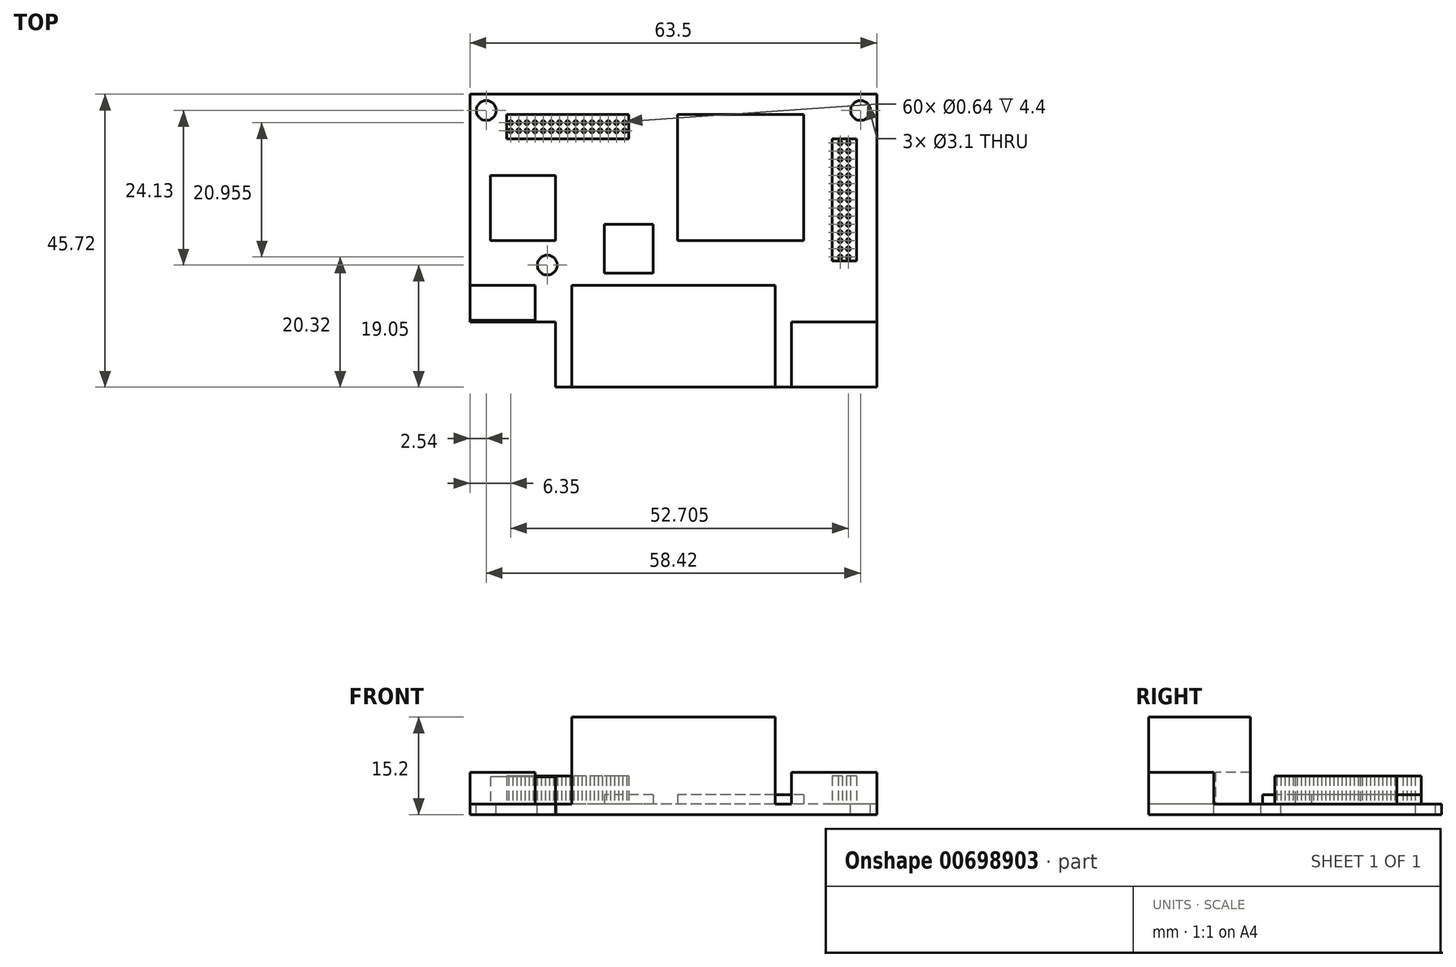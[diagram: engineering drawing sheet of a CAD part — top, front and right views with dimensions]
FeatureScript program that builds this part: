
annotation { "Feature Type Name" : "Feature", "Feature Type Description" : "" }
export const myFeature = defineFeature(function(context is Context, id is Id, definition is map)
    precondition{}
    {
        {
            var Q0;
            Q0=qCreatedBy(makeId("Top.planeOp"),FACE);
            var sketch = newSketch(context, id + "F0", { "sketchPlane" : qUnion([Q0])});
            skLineSegment(sketch, "E0.bottom", {"start": v(31.75, 22.86) * mm, "end": v(-31.75, 22.86) * mm});
            skLineSegment(sketch, "E0.top", {"start": v(31.75, -22.86) * mm, "end": v(-31.75, -22.86) * mm});
            skLineSegment(sketch, "E0.left", {"start": v(31.75, 22.86) * mm, "end": v(31.75, -22.86) * mm});
            skLineSegment(sketch, "E0.right", {"start": v(-31.75, 22.86) * mm, "end": v(-31.75, -22.86) * mm});
            skPoint(sketch, "E0.middle", {"position": v(0, 0) * mm});
            skCircle(sketch, "E1", {"center": v(-29.21, 20.32) * mm, "radius": 1.55 * mm});
            skCircle(sketch, "E2", {"center": v(29.21, 20.32) * mm, "radius": 1.55 * mm});
            skCircle(sketch, "E3", {"center": v(-19.69, -3.81) * mm, "radius": 1.55 * mm});
            skLineSegment(sketch, "E4.bottom", {"start": v(-18.41, 10.16) * mm, "end": v(-28.57, 10.16) * mm});
            skLineSegment(sketch, "E4.top", {"start": v(-18.41, 0) * mm, "end": v(-28.57, 0) * mm});
            skLineSegment(sketch, "E4.left", {"start": v(-18.41, 10.16) * mm, "end": v(-18.41, 0) * mm});
            skLineSegment(sketch, "E4.right", {"start": v(-28.57, 10.16) * mm, "end": v(-28.57, 0) * mm});
            skPoint(sketch, "E4.middle", {"position": v(-23.5, 5.08) * mm});
            skLineSegment(sketch, "E5.bottom", {"start": v(20.32, 19.69) * mm, "end": v(0.63, 19.69) * mm});
            skLineSegment(sketch, "E5.top", {"start": v(20.32, 0) * mm, "end": v(0.63, 0) * mm});
            skLineSegment(sketch, "E5.left", {"start": v(20.32, 19.69) * mm, "end": v(20.32, 0) * mm});
            skLineSegment(sketch, "E5.right", {"start": v(0.64, 19.69) * mm, "end": v(0.64, 0) * mm});
            skPoint(sketch, "E5.middle", {"position": v(10.48, 9.84) * mm});
            skLineSegment(sketch, "E6.bottom", {"start": v(-3.17, 2.54) * mm, "end": v(-10.8, 2.54) * mm});
            skLineSegment(sketch, "E6.top", {"start": v(-3.17, -5.08) * mm, "end": v(-10.8, -5.08) * mm});
            skLineSegment(sketch, "E6.left", {"start": v(-3.17, 2.54) * mm, "end": v(-3.17, -5.08) * mm});
            skLineSegment(sketch, "E6.right", {"start": v(-10.8, 2.54) * mm, "end": v(-10.8, -5.08) * mm});
            skPoint(sketch, "E6.middle", {"position": v(-6.98, -1.27) * mm});
            skLineSegment(sketch, "E7.bottom", {"start": v(-31.75, -22.86) * mm, "end": v(-18.41, -22.86) * mm});
            skLineSegment(sketch, "E7.top", {"start": v(-31.75, -12.7) * mm, "end": v(-18.42, -12.7) * mm});
            skLineSegment(sketch, "E7.left", {"start": v(-31.75, -22.86) * mm, "end": v(-31.75, -12.7) * mm});
            skLineSegment(sketch, "E7.right", {"start": v(-18.41, -22.86) * mm, "end": v(-18.41, -12.7) * mm});
            skPoint(sketch, "E7.middle", {"position": v(-25.08, -17.78) * mm});
            skLineSegment(sketch, "E8.bottom", {"start": v(-21.6, -6.99) * mm, "end": v(-31.75, -6.99) * mm});
            skLineSegment(sketch, "E8.top", {"start": v(-21.59, -12.45) * mm, "end": v(-31.75, -12.45) * mm});
            skLineSegment(sketch, "E8.left", {"start": v(-21.59, -6.99) * mm, "end": v(-21.59, -12.45) * mm});
            skLineSegment(sketch, "E8.right", {"start": v(-31.75, -6.99) * mm, "end": v(-31.75, -12.45) * mm});
            skPoint(sketch, "E8.middle", {"position": v(-26.67, -9.72) * mm});
            skLineSegment(sketch, "E9.bottom", {"start": v(31.75, -12.7) * mm, "end": v(18.41, -12.7) * mm});
            skLineSegment(sketch, "E9.top", {"start": v(31.75, -22.86) * mm, "end": v(18.41, -22.86) * mm});
            skLineSegment(sketch, "E9.left", {"start": v(31.75, -12.7) * mm, "end": v(31.75, -22.86) * mm});
            skLineSegment(sketch, "E9.right", {"start": v(18.41, -12.7) * mm, "end": v(18.41, -22.86) * mm});
            skPoint(sketch, "E9.middle", {"position": v(25.08, -17.78) * mm});
            skLineSegment(sketch, "E10.bottom", {"start": v(15.88, -6.99) * mm, "end": v(-15.88, -6.99) * mm});
            skLineSegment(sketch, "E10.top", {"start": v(15.88, -22.86) * mm, "end": v(-15.88, -22.86) * mm});
            skLineSegment(sketch, "E10.left", {"start": v(15.88, -6.99) * mm, "end": v(15.88, -22.86) * mm});
            skLineSegment(sketch, "E10.right", {"start": v(-15.88, -6.99) * mm, "end": v(-15.88, -22.86) * mm});
            skPoint(sketch, "E10.middle", {"position": v(0, -14.92) * mm});
            skCircle(sketch, "E11", {"center": v(-25.4, 18.41) * mm, "radius": 0.32 * mm});
            skCircle(sketch, "E12.1.0.0", {"center": v(-24.13, 18.41) * mm, "radius": 0.32 * mm});
            skCircle(sketch, "E12.2.0.0", {"center": v(-22.86, 18.41) * mm, "radius": 0.32 * mm});
            skCircle(sketch, "E12.3.0.0", {"center": v(-21.59, 18.41) * mm, "radius": 0.32 * mm});
            skCircle(sketch, "E12.4.0.0", {"center": v(-20.32, 18.41) * mm, "radius": 0.32 * mm});
            skCircle(sketch, "E12.5.0.0", {"center": v(-19.05, 18.41) * mm, "radius": 0.32 * mm});
            skCircle(sketch, "E12.6.0.0", {"center": v(-17.78, 18.41) * mm, "radius": 0.32 * mm});
            skCircle(sketch, "E12.7.0.0", {"center": v(-16.51, 18.41) * mm, "radius": 0.32 * mm});
            skCircle(sketch, "E12.8.0.0", {"center": v(-15.24, 18.41) * mm, "radius": 0.32 * mm});
            skCircle(sketch, "E12.9.0.0", {"center": v(-13.97, 18.41) * mm, "radius": 0.32 * mm});
            skCircle(sketch, "E12.10.0.0", {"center": v(-12.7, 18.41) * mm, "radius": 0.32 * mm});
            skCircle(sketch, "E12.11.0.0", {"center": v(-11.43, 18.41) * mm, "radius": 0.32 * mm});
            skCircle(sketch, "E12.12.0.0", {"center": v(-10.16, 18.41) * mm, "radius": 0.32 * mm});
            skCircle(sketch, "E12.13.0.0", {"center": v(-8.89, 18.41) * mm, "radius": 0.32 * mm});
            skCircle(sketch, "E12.14.0.0", {"center": v(-7.62, 18.41) * mm, "radius": 0.32 * mm});
            skLineSegment(sketch, "E12.direction1", {"start": v(-25.4, 18.41) * mm, "end": v(-24.13, 18.41) * mm, "construction": true});
            skCircle(sketch, "E13.1.0.0", {"center": v(-19.05, 17.14) * mm, "radius": 0.32 * mm});
            skCircle(sketch, "E13.1.0.1", {"center": v(-17.78, 17.14) * mm, "radius": 0.32 * mm});
            skCircle(sketch, "E13.1.0.2", {"center": v(-16.51, 17.14) * mm, "radius": 0.32 * mm});
            skCircle(sketch, "E13.1.0.3", {"center": v(-13.97, 17.14) * mm, "radius": 0.32 * mm});
            skCircle(sketch, "E13.1.0.4", {"center": v(-11.43, 17.14) * mm, "radius": 0.32 * mm});
            skCircle(sketch, "E13.1.0.5", {"center": v(-8.89, 17.14) * mm, "radius": 0.32 * mm});
            skCircle(sketch, "E13.1.0.6", {"center": v(-25.4, 17.15) * mm, "radius": 0.32 * mm});
            skCircle(sketch, "E13.1.0.7", {"center": v(-24.13, 17.15) * mm, "radius": 0.32 * mm});
            skCircle(sketch, "E13.1.0.8", {"center": v(-22.86, 17.14) * mm, "radius": 0.32 * mm});
            skCircle(sketch, "E13.1.0.9", {"center": v(-21.59, 17.14) * mm, "radius": 0.32 * mm});
            skCircle(sketch, "E13.1.0.10", {"center": v(-20.32, 17.14) * mm, "radius": 0.32 * mm});
            skLineSegment(sketch, "E13.1.0.11", {"start": v(-25.4, 17.14) * mm, "end": v(-24.13, 17.14) * mm, "construction": true});
            skCircle(sketch, "E13.1.0.12", {"center": v(-7.62, 17.14) * mm, "radius": 0.32 * mm});
            skCircle(sketch, "E13.1.0.13", {"center": v(-10.16, 17.14) * mm, "radius": 0.32 * mm});
            skCircle(sketch, "E13.1.0.14", {"center": v(-12.7, 17.14) * mm, "radius": 0.32 * mm});
            skCircle(sketch, "E13.1.0.15", {"center": v(-15.24, 17.14) * mm, "radius": 0.32 * mm});
            skLineSegment(sketch, "E13.direction1", {"start": v(-25.4, 18.41) * mm, "end": v(-25.4, 17.15) * mm, "construction": true});
            skCircle(sketch, "E14", {"center": v(26.04, -2.54) * mm, "radius": 0.32 * mm});
            skCircle(sketch, "E15.1.0.0", {"center": v(26.03, -1.27) * mm, "radius": 0.32 * mm});
            skCircle(sketch, "E15.2.0.0", {"center": v(26.04, 0) * mm, "radius": 0.32 * mm});
            skCircle(sketch, "E15.3.0.0", {"center": v(26.04, 1.27) * mm, "radius": 0.32 * mm});
            skCircle(sketch, "E15.4.0.0", {"center": v(26.04, 2.54) * mm, "radius": 0.32 * mm});
            skCircle(sketch, "E15.5.0.0", {"center": v(26.04, 3.8) * mm, "radius": 0.32 * mm});
            skCircle(sketch, "E15.6.0.0", {"center": v(26.04, 5.08) * mm, "radius": 0.32 * mm});
            skCircle(sketch, "E15.7.0.0", {"center": v(26.04, 6.35) * mm, "radius": 0.32 * mm});
            skCircle(sketch, "E15.8.0.0", {"center": v(26.04, 7.62) * mm, "radius": 0.32 * mm});
            skCircle(sketch, "E15.9.0.0", {"center": v(26.04, 8.89) * mm, "radius": 0.32 * mm});
            skCircle(sketch, "E15.10.0.0", {"center": v(26.04, 10.16) * mm, "radius": 0.32 * mm});
            skCircle(sketch, "E15.11.0.0", {"center": v(26.04, 11.43) * mm, "radius": 0.32 * mm});
            skCircle(sketch, "E15.12.0.0", {"center": v(26.04, 12.7) * mm, "radius": 0.32 * mm});
            skCircle(sketch, "E15.13.0.0", {"center": v(26.04, 13.97) * mm, "radius": 0.32 * mm});
            skCircle(sketch, "E15.14.0.0", {"center": v(26.04, 15.24) * mm, "radius": 0.32 * mm});
            skLineSegment(sketch, "E15.direction1", {"start": v(26.04, -2.54) * mm, "end": v(26.04, -1.27) * mm, "construction": true});
            skCircle(sketch, "E16.1.0.0", {"center": v(27.3, 3.8) * mm, "radius": 0.32 * mm});
            skCircle(sketch, "E16.1.0.1", {"center": v(27.3, 5.08) * mm, "radius": 0.32 * mm});
            skCircle(sketch, "E16.1.0.2", {"center": v(27.3, 6.35) * mm, "radius": 0.32 * mm});
            skCircle(sketch, "E16.1.0.3", {"center": v(27.3, 8.89) * mm, "radius": 0.32 * mm});
            skCircle(sketch, "E16.1.0.4", {"center": v(27.3, 11.43) * mm, "radius": 0.32 * mm});
            skCircle(sketch, "E16.1.0.5", {"center": v(27.3, 13.97) * mm, "radius": 0.32 * mm});
            skCircle(sketch, "E16.1.0.6", {"center": v(27.3, -2.54) * mm, "radius": 0.32 * mm});
            skCircle(sketch, "E16.1.0.7", {"center": v(27.3, -1.27) * mm, "radius": 0.32 * mm});
            skCircle(sketch, "E16.1.0.8", {"center": v(27.3, 0) * mm, "radius": 0.32 * mm});
            skCircle(sketch, "E16.1.0.9", {"center": v(27.3, 1.27) * mm, "radius": 0.32 * mm});
            skCircle(sketch, "E16.1.0.10", {"center": v(27.3, 2.54) * mm, "radius": 0.32 * mm});
            skLineSegment(sketch, "E16.1.0.11", {"start": v(27.3, -2.54) * mm, "end": v(27.3, -1.27) * mm, "construction": true});
            skCircle(sketch, "E16.1.0.12", {"center": v(27.3, 15.24) * mm, "radius": 0.32 * mm});
            skCircle(sketch, "E16.1.0.13", {"center": v(27.3, 12.7) * mm, "radius": 0.32 * mm});
            skCircle(sketch, "E16.1.0.14", {"center": v(27.3, 10.16) * mm, "radius": 0.32 * mm});
            skCircle(sketch, "E16.1.0.15", {"center": v(27.3, 7.62) * mm, "radius": 0.32 * mm});
            skLineSegment(sketch, "E16.direction1", {"start": v(26.04, -2.54) * mm, "end": v(27.3, -2.54) * mm, "construction": true});
            skLineSegment(sketch, "E17.bottom", {"start": v(-6.98, 19.69) * mm, "end": v(-26.04, 19.69) * mm});
            skLineSegment(sketch, "E17.top", {"start": v(-6.98, 15.87) * mm, "end": v(-26.04, 15.87) * mm});
            skLineSegment(sketch, "E17.left", {"start": v(-6.98, 19.69) * mm, "end": v(-6.98, 15.87) * mm});
            skLineSegment(sketch, "E17.right", {"start": v(-26.04, 19.69) * mm, "end": v(-26.04, 15.87) * mm});
            skPoint(sketch, "E17.middle", {"position": v(-16.5, 17.78) * mm});
            skLineSegment(sketch, "E18.bottom", {"start": v(28.58, 15.87) * mm, "end": v(24.77, 15.87) * mm});
            skLineSegment(sketch, "E18.top", {"start": v(28.58, -3.18) * mm, "end": v(24.77, -3.18) * mm});
            skLineSegment(sketch, "E18.left", {"start": v(28.58, 15.87) * mm, "end": v(28.58, -3.18) * mm});
            skLineSegment(sketch, "E18.right", {"start": v(24.77, 15.87) * mm, "end": v(24.77, -3.18) * mm});
            skPoint(sketch, "E18.middle", {"position": v(26.67, 6.35) * mm});
            skSolve(sketch);
        }
        {
            var Q0;
            Q0=makeQuery(id+"F0.imprint","IMPRINT",FACE,{"disambiguationData":[TD([[makeQuery(id+"F0.imprint","IMPRINT",EDGE,{"derivedFrom":sQuery(id+"F0.wireOp",EDGE,"E14")}),-1.0]])]});
            var Q1;
            Q1=makeQuery(id+"F0.imprint","IMPRINT",FACE,{"disambiguationData":[TD([[makeQuery(id+"F0.imprint","IMPRINT",EDGE,{"derivedFrom":sQuery(id+"F0.wireOp",EDGE,"E4.bottom")}),1.0]])]});
            var Q2;
            Q2=makeQuery(id+"F0.imprint","IMPRINT",FACE,{"disambiguationData":[TD([[makeQuery(id+"F0.imprint","IMPRINT",EDGE,{"derivedFrom":sQuery(id+"F0.wireOp",EDGE,"E5.bottom")}),1.0]])]});
            var Q3;
            Q3=makeQuery(id+"F0.imprint","IMPRINT",FACE,{"disambiguationData":[TD([[makeQuery(id+"F0.imprint","IMPRINT",EDGE,{"derivedFrom":sQuery(id+"F0.wireOp",EDGE,"E8.bottom")}),1.0]])]});
            var Q4;
            Q4=makeQuery(id+"F0.imprint","IMPRINT",FACE,{"disambiguationData":[TD([[makeQuery(id+"F0.imprint","IMPRINT",EDGE,{"derivedFrom":sQuery(id+"F0.wireOp",EDGE,"E7.bottom")}),1.0]])]});
            var Q5;
            Q5=makeQuery(id+"F0.imprint","IMPRINT",FACE,{"disambiguationData":[TD([[makeQuery(id+"F0.imprint","IMPRINT",EDGE,{"derivedFrom":sQuery(id+"F0.wireOp",EDGE,"E11")}),-1.0]])]});
            var Q6;
            {var subQ7=sQuery(id+"F0.wireOp",EDGE,"E0.bottom");Q6=makeQuery(id+"F0.imprint","IMPRINT",FACE,{"disambiguationData":[TD([[makeQuery(id+"F0.imprint","IMPRINT",EDGE,{"derivedFrom":subQ7}),1.0]])]});}
            var Q7;
            Q7=makeQuery(id+"F0.imprint","IMPRINT",FACE,{"disambiguationData":[TD([[makeQuery(id+"F0.imprint","IMPRINT",EDGE,{"derivedFrom":sQuery(id+"F0.wireOp",EDGE,"E6.bottom")}),1.0]])]});
            var Q8;
            Q8=makeQuery(id+"F0.imprint","IMPRINT",FACE,{"disambiguationData":[TD([[makeQuery(id+"F0.imprint","IMPRINT",EDGE,{"derivedFrom":sQuery(id+"F0.wireOp",EDGE,"E10.bottom")}),1.0]])]});
            var Q9;
            Q9=makeQuery(id+"F0.imprint","IMPRINT",FACE,{"disambiguationData":[TD([[makeQuery(id+"F0.imprint","IMPRINT",EDGE,{"derivedFrom":sQuery(id+"F0.wireOp",EDGE,"E9.bottom")}),1.0]])]});
            var Q10;
            Q10=makeQuery(id+"F0.imprint","IMPRINT",FACE,{"disambiguationData":[TD([[makeQuery(id+"F0.imprint","IMPRINT",EDGE,{"derivedFrom":sQuery(id+"F0.wireOp",EDGE,"E16.1.0.4")}),1.0]])]});
            var Q11;
            Q11=makeQuery(id+"F0.imprint","IMPRINT",FACE,{"disambiguationData":[TD([[makeQuery(id+"F0.imprint","IMPRINT",EDGE,{"derivedFrom":sQuery(id+"F0.wireOp",EDGE,"E16.1.0.1")}),1.0]])]});
            var Q12;
            Q12=makeQuery(id+"F0.imprint","IMPRINT",FACE,{"disambiguationData":[TD([[makeQuery(id+"F0.imprint","IMPRINT",EDGE,{"derivedFrom":sQuery(id+"F0.wireOp",EDGE,"E15.8.0.0")}),1.0]])]});
            var Q13;
            Q13=makeQuery(id+"F0.imprint","IMPRINT",FACE,{"disambiguationData":[TD([[makeQuery(id+"F0.imprint","IMPRINT",EDGE,{"derivedFrom":sQuery(id+"F0.wireOp",EDGE,"E15.11.0.0")}),1.0]])]});
            var Q14;
            Q14=makeQuery(id+"F0.imprint","IMPRINT",FACE,{"disambiguationData":[TD([[makeQuery(id+"F0.imprint","IMPRINT",EDGE,{"derivedFrom":sQuery(id+"F0.wireOp",EDGE,"E12.10.0.0")}),1.0]])]});
            var Q15;
            Q15=makeQuery(id+"F0.imprint","IMPRINT",FACE,{"disambiguationData":[TD([[makeQuery(id+"F0.imprint","IMPRINT",EDGE,{"derivedFrom":sQuery(id+"F0.wireOp",EDGE,"E13.1.0.8")}),1.0]])]});
            var Q16;
            Q16=makeQuery(id+"F0.imprint","IMPRINT",FACE,{"disambiguationData":[TD([[makeQuery(id+"F0.imprint","IMPRINT",EDGE,{"derivedFrom":sQuery(id+"F0.wireOp",EDGE,"E15.7.0.0")}),1.0]])]});
            var Q17;
            Q17=makeQuery(id+"F0.imprint","IMPRINT",FACE,{"disambiguationData":[TD([[makeQuery(id+"F0.imprint","IMPRINT",EDGE,{"derivedFrom":sQuery(id+"F0.wireOp",EDGE,"E12.14.0.0")}),1.0]])]});
            var Q18;
            Q18=makeQuery(id+"F0.imprint","IMPRINT",FACE,{"disambiguationData":[TD([[makeQuery(id+"F0.imprint","IMPRINT",EDGE,{"derivedFrom":sQuery(id+"F0.wireOp",EDGE,"E15.6.0.0")}),1.0]])]});
            var Q19;
            Q19=makeQuery(id+"F0.imprint","IMPRINT",FACE,{"disambiguationData":[TD([[makeQuery(id+"F0.imprint","IMPRINT",EDGE,{"derivedFrom":sQuery(id+"F0.wireOp",EDGE,"E12.12.0.0")}),1.0]])]});
            var Q20;
            Q20=makeQuery(id+"F0.imprint","IMPRINT",FACE,{"disambiguationData":[TD([[makeQuery(id+"F0.imprint","IMPRINT",EDGE,{"derivedFrom":sQuery(id+"F0.wireOp",EDGE,"E13.1.0.1")}),1.0]])]});
            var Q21;
            Q21=makeQuery(id+"F0.imprint","IMPRINT",FACE,{"disambiguationData":[TD([[makeQuery(id+"F0.imprint","IMPRINT",EDGE,{"derivedFrom":sQuery(id+"F0.wireOp",EDGE,"E12.3.0.0")}),1.0]])]});
            var Q22;
            Q22=makeQuery(id+"F0.imprint","IMPRINT",FACE,{"disambiguationData":[TD([[makeQuery(id+"F0.imprint","IMPRINT",EDGE,{"derivedFrom":sQuery(id+"F0.wireOp",EDGE,"E13.1.0.12")}),1.0]])]});
            var Q23;
            Q23=makeQuery(id+"F0.imprint","IMPRINT",FACE,{"disambiguationData":[TD([[makeQuery(id+"F0.imprint","IMPRINT",EDGE,{"derivedFrom":sQuery(id+"F0.wireOp",EDGE,"E13.1.0.2")}),1.0]])]});
            var Q24;
            Q24=makeQuery(id+"F0.imprint","IMPRINT",FACE,{"disambiguationData":[TD([[makeQuery(id+"F0.imprint","IMPRINT",EDGE,{"derivedFrom":sQuery(id+"F0.wireOp",EDGE,"E12.13.0.0")}),1.0]])]});
            var Q25;
            Q25=makeQuery(id+"F0.imprint","IMPRINT",FACE,{"disambiguationData":[TD([[makeQuery(id+"F0.imprint","IMPRINT",EDGE,{"derivedFrom":sQuery(id+"F0.wireOp",EDGE,"E15.2.0.0")}),1.0]])]});
            var Q26;
            Q26=makeQuery(id+"F0.imprint","IMPRINT",FACE,{"disambiguationData":[TD([[makeQuery(id+"F0.imprint","IMPRINT",EDGE,{"derivedFrom":sQuery(id+"F0.wireOp",EDGE,"E16.1.0.13")}),1.0]])]});
            var Q27;
            Q27=makeQuery(id+"F0.imprint","IMPRINT",FACE,{"disambiguationData":[TD([[makeQuery(id+"F0.imprint","IMPRINT",EDGE,{"derivedFrom":sQuery(id+"F0.wireOp",EDGE,"E13.1.0.0")}),1.0]])]});
            var Q28;
            Q28=makeQuery(id+"F0.imprint","IMPRINT",FACE,{"disambiguationData":[TD([[makeQuery(id+"F0.imprint","IMPRINT",EDGE,{"derivedFrom":sQuery(id+"F0.wireOp",EDGE,"E16.1.0.14")}),1.0]])]});
            var Q29;
            Q29=makeQuery(id+"F0.imprint","IMPRINT",FACE,{"disambiguationData":[TD([[makeQuery(id+"F0.imprint","IMPRINT",EDGE,{"derivedFrom":sQuery(id+"F0.wireOp",EDGE,"E15.12.0.0")}),1.0]])]});
            var Q30;
            Q30=makeQuery(id+"F0.imprint","IMPRINT",FACE,{"disambiguationData":[TD([[makeQuery(id+"F0.imprint","IMPRINT",EDGE,{"derivedFrom":sQuery(id+"F0.wireOp",EDGE,"E15.3.0.0")}),1.0]])]});
            var Q31;
            Q31=makeQuery(id+"F0.imprint","IMPRINT",FACE,{"disambiguationData":[TD([[makeQuery(id+"F0.imprint","IMPRINT",EDGE,{"derivedFrom":sQuery(id+"F0.wireOp",EDGE,"E12.11.0.0")}),1.0]])]});
            var Q32;
            Q32=makeQuery(id+"F0.imprint","IMPRINT",FACE,{"disambiguationData":[TD([[makeQuery(id+"F0.imprint","IMPRINT",EDGE,{"derivedFrom":sQuery(id+"F0.wireOp",EDGE,"E15.13.0.0")}),1.0]])]});
            var Q33;
            Q33=makeQuery(id+"F0.imprint","IMPRINT",FACE,{"disambiguationData":[TD([[makeQuery(id+"F0.imprint","IMPRINT",EDGE,{"derivedFrom":sQuery(id+"F0.wireOp",EDGE,"E12.2.0.0")}),1.0]])]});
            var Q34;
            Q34=makeQuery(id+"F0.imprint","IMPRINT",FACE,{"disambiguationData":[TD([[makeQuery(id+"F0.imprint","IMPRINT",EDGE,{"derivedFrom":sQuery(id+"F0.wireOp",EDGE,"E15.10.0.0")}),1.0]])]});
            var Q35;
            Q35=makeQuery(id+"F0.imprint","IMPRINT",FACE,{"disambiguationData":[TD([[makeQuery(id+"F0.imprint","IMPRINT",EDGE,{"derivedFrom":sQuery(id+"F0.wireOp",EDGE,"E13.1.0.9")}),1.0]])]});
            var Q36;
            Q36=makeQuery(id+"F0.imprint","IMPRINT",FACE,{"disambiguationData":[TD([[makeQuery(id+"F0.imprint","IMPRINT",EDGE,{"derivedFrom":sQuery(id+"F0.wireOp",EDGE,"E16.1.0.9")}),1.0]])]});
            var Q37;
            Q37=makeQuery(id+"F0.imprint","IMPRINT",FACE,{"disambiguationData":[TD([[makeQuery(id+"F0.imprint","IMPRINT",EDGE,{"derivedFrom":sQuery(id+"F0.wireOp",EDGE,"E16.1.0.5")}),1.0]])]});
            var Q38;
            Q38=makeQuery(id+"F0.imprint","IMPRINT",FACE,{"disambiguationData":[TD([[makeQuery(id+"F0.imprint","IMPRINT",EDGE,{"derivedFrom":sQuery(id+"F0.wireOp",EDGE,"E12.6.0.0")}),1.0]])]});
            var Q39;
            Q39=makeQuery(id+"F0.imprint","IMPRINT",FACE,{"disambiguationData":[TD([[makeQuery(id+"F0.imprint","IMPRINT",EDGE,{"derivedFrom":sQuery(id+"F0.wireOp",EDGE,"E15.14.0.0")}),1.0]])]});
            var Q40;
            Q40=makeQuery(id+"F0.imprint","IMPRINT",FACE,{"disambiguationData":[TD([[makeQuery(id+"F0.imprint","IMPRINT",EDGE,{"derivedFrom":sQuery(id+"F0.wireOp",EDGE,"E16.1.0.8")}),1.0]])]});
            var Q41;
            Q41=makeQuery(id+"F0.imprint","IMPRINT",FACE,{"disambiguationData":[TD([[makeQuery(id+"F0.imprint","IMPRINT",EDGE,{"derivedFrom":sQuery(id+"F0.wireOp",EDGE,"E13.1.0.10")}),1.0]])]});
            var Q42;
            Q42=makeQuery(id+"F0.imprint","IMPRINT",FACE,{"disambiguationData":[TD([[makeQuery(id+"F0.imprint","IMPRINT",EDGE,{"derivedFrom":sQuery(id+"F0.wireOp",EDGE,"E12.5.0.0")}),1.0]])]});
            var Q43;
            Q43=makeQuery(id+"F0.imprint","IMPRINT",FACE,{"disambiguationData":[TD([[makeQuery(id+"F0.imprint","IMPRINT",EDGE,{"derivedFrom":sQuery(id+"F0.wireOp",EDGE,"E16.1.0.3")}),1.0]])]});
            var Q44;
            Q44=makeQuery(id+"F0.imprint","IMPRINT",FACE,{"disambiguationData":[TD([[makeQuery(id+"F0.imprint","IMPRINT",EDGE,{"derivedFrom":sQuery(id+"F0.wireOp",EDGE,"E15.5.0.0")}),1.0]])]});
            var Q45;
            Q45=makeQuery(id+"F0.imprint","IMPRINT",FACE,{"disambiguationData":[TD([[makeQuery(id+"F0.imprint","IMPRINT",EDGE,{"derivedFrom":sQuery(id+"F0.wireOp",EDGE,"E12.7.0.0")}),1.0]])]});
            var Q46;
            Q46=makeQuery(id+"F0.imprint","IMPRINT",FACE,{"disambiguationData":[TD([[makeQuery(id+"F0.imprint","IMPRINT",EDGE,{"derivedFrom":sQuery(id+"F0.wireOp",EDGE,"E15.9.0.0")}),1.0]])]});
            var Q47;
            Q47=makeQuery(id+"F0.imprint","IMPRINT",FACE,{"disambiguationData":[TD([[makeQuery(id+"F0.imprint","IMPRINT",EDGE,{"derivedFrom":sQuery(id+"F0.wireOp",EDGE,"E16.1.0.10")}),1.0]])]});
            var Q48;
            Q48=makeQuery(id+"F0.imprint","IMPRINT",FACE,{"disambiguationData":[TD([[makeQuery(id+"F0.imprint","IMPRINT",EDGE,{"derivedFrom":sQuery(id+"F0.wireOp",EDGE,"E13.1.0.5")}),1.0]])]});
            var Q49;
            Q49=makeQuery(id+"F0.imprint","IMPRINT",FACE,{"disambiguationData":[TD([[makeQuery(id+"F0.imprint","IMPRINT",EDGE,{"derivedFrom":sQuery(id+"F0.wireOp",EDGE,"E15.4.0.0")}),1.0]])]});
            var Q50;
            Q50=makeQuery(id+"F0.imprint","IMPRINT",FACE,{"disambiguationData":[TD([[makeQuery(id+"F0.imprint","IMPRINT",EDGE,{"derivedFrom":sQuery(id+"F0.wireOp",EDGE,"E13.1.0.13")}),1.0]])]});
            var Q51;
            Q51=makeQuery(id+"F0.imprint","IMPRINT",FACE,{"disambiguationData":[TD([[makeQuery(id+"F0.imprint","IMPRINT",EDGE,{"derivedFrom":sQuery(id+"F0.wireOp",EDGE,"E16.1.0.2")}),1.0]])]});
            var Q52;
            Q52=makeQuery(id+"F0.imprint","IMPRINT",FACE,{"disambiguationData":[TD([[makeQuery(id+"F0.imprint","IMPRINT",EDGE,{"derivedFrom":sQuery(id+"F0.wireOp",EDGE,"E13.1.0.15")}),1.0]])]});
            var Q53;
            Q53=makeQuery(id+"F0.imprint","IMPRINT",FACE,{"disambiguationData":[TD([[makeQuery(id+"F0.imprint","IMPRINT",EDGE,{"derivedFrom":sQuery(id+"F0.wireOp",EDGE,"E13.1.0.3")}),1.0]])]});
            var Q54;
            Q54=makeQuery(id+"F0.imprint","IMPRINT",FACE,{"disambiguationData":[TD([[makeQuery(id+"F0.imprint","IMPRINT",EDGE,{"derivedFrom":sQuery(id+"F0.wireOp",EDGE,"E16.1.0.15")}),1.0]])]});
            var Q55;
            Q55=makeQuery(id+"F0.imprint","IMPRINT",FACE,{"disambiguationData":[TD([[makeQuery(id+"F0.imprint","IMPRINT",EDGE,{"derivedFrom":sQuery(id+"F0.wireOp",EDGE,"E13.1.0.4")}),1.0]])]});
            var Q56;
            Q56=makeQuery(id+"F0.imprint","IMPRINT",FACE,{"disambiguationData":[TD([[makeQuery(id+"F0.imprint","IMPRINT",EDGE,{"derivedFrom":sQuery(id+"F0.wireOp",EDGE,"E12.9.0.0")}),1.0]])]});
            var Q57;
            Q57=makeQuery(id+"F0.imprint","IMPRINT",FACE,{"disambiguationData":[TD([[makeQuery(id+"F0.imprint","IMPRINT",EDGE,{"derivedFrom":sQuery(id+"F0.wireOp",EDGE,"E13.1.0.14")}),1.0]])]});
            var Q58;
            Q58=makeQuery(id+"F0.imprint","IMPRINT",FACE,{"disambiguationData":[TD([[makeQuery(id+"F0.imprint","IMPRINT",EDGE,{"derivedFrom":sQuery(id+"F0.wireOp",EDGE,"E12.4.0.0")}),1.0]])]});
            var Q59;
            Q59=makeQuery(id+"F0.imprint","IMPRINT",FACE,{"disambiguationData":[TD([[makeQuery(id+"F0.imprint","IMPRINT",EDGE,{"derivedFrom":sQuery(id+"F0.wireOp",EDGE,"E16.1.0.0")}),1.0]])]});
            var Q60;
            Q60=makeQuery(id+"F0.imprint","IMPRINT",FACE,{"disambiguationData":[TD([[makeQuery(id+"F0.imprint","IMPRINT",EDGE,{"derivedFrom":sQuery(id+"F0.wireOp",EDGE,"E12.8.0.0")}),1.0]])]});
            var Q61;
            Q61=makeQuery(id+"F0.imprint","IMPRINT",FACE,{"disambiguationData":[TD([[makeQuery(id+"F0.imprint","IMPRINT",EDGE,{"derivedFrom":sQuery(id+"F0.wireOp",EDGE,"E16.1.0.12")}),1.0]])]});
            var Q62;
            Q62=makeQuery(id+"F0.imprint","IMPRINT",FACE,{"disambiguationData":[TD([[makeQuery(id+"F0.imprint","IMPRINT",EDGE,{"derivedFrom":sQuery(id+"F0.wireOp",EDGE,"E15.1.0.0")}),1.0]])]});
            var Q63;
            Q63=makeQuery(id+"F0.imprint","IMPRINT",FACE,{"disambiguationData":[TD([[makeQuery(id+"F0.imprint","IMPRINT",EDGE,{"derivedFrom":sQuery(id+"F0.wireOp",EDGE,"E16.1.0.7")}),1.0]])]});
            var Q64;
            Q64=makeQuery(id+"F0.imprint","IMPRINT",FACE,{"disambiguationData":[TD([[makeQuery(id+"F0.imprint","IMPRINT",EDGE,{"derivedFrom":sQuery(id+"F0.wireOp",EDGE,"E13.1.0.7")}),1.0]])]});
            var Q65;
            Q65=makeQuery(id+"F0.imprint","IMPRINT",FACE,{"disambiguationData":[TD([[makeQuery(id+"F0.imprint","IMPRINT",EDGE,{"derivedFrom":sQuery(id+"F0.wireOp",EDGE,"E12.1.0.0")}),1.0]])]});
            var Q66;
            Q66=makeQuery(id+"F0.imprint","IMPRINT",FACE,{"disambiguationData":[TD([[makeQuery(id+"F0.imprint","IMPRINT",EDGE,{"derivedFrom":sQuery(id+"F0.wireOp",EDGE,"E13.1.0.6")}),1.0]])]});
            var Q67;
            Q67=makeQuery(id+"F0.imprint","IMPRINT",FACE,{"disambiguationData":[TD([[makeQuery(id+"F0.imprint","IMPRINT",EDGE,{"derivedFrom":sQuery(id+"F0.wireOp",EDGE,"E14")}),1.0]])]});
            var Q68;
            Q68=makeQuery(id+"F0.imprint","IMPRINT",FACE,{"disambiguationData":[TD([[makeQuery(id+"F0.imprint","IMPRINT",EDGE,{"derivedFrom":sQuery(id+"F0.wireOp",EDGE,"E11")}),1.0]])]});
            var Q69;
            Q69=makeQuery(id+"F0.imprint","IMPRINT",FACE,{"disambiguationData":[TD([[makeQuery(id+"F0.imprint","IMPRINT",EDGE,{"derivedFrom":sQuery(id+"F0.wireOp",EDGE,"E16.1.0.6")}),1.0]])]});
            extrude(context, id + "F1", {"entities" : qUnion([Q0, Q1, Q2, Q3, Q4, Q5, Q6, Q7, Q8, Q9, Q10, Q11, Q12, Q13, Q14, Q15, Q16, Q17, Q18, Q19, Q20, Q21, Q22, Q23, Q24, Q25, Q26, Q27, Q28, Q29, Q30, Q31, Q32, Q33, Q34, Q35, Q36, Q37, Q38, Q39, Q40, Q41, Q42, Q43, Q44, Q45, Q46, Q47, Q48, Q49, Q50, Q51, Q52, Q53, Q54, Q55, Q56, Q57, Q58, Q59, Q60, Q61, Q62, Q63, Q64, Q65, Q66, Q67, Q68, Q69]), "oppositeDirection" : true, "depth" : 1.6 * mm});
        }
        {
            var Q0;
            Q0=makeQuery(id+"F0.imprint","IMPRINT",FACE,{"disambiguationData":[TD([[makeQuery(id+"F0.imprint","IMPRINT",EDGE,{"derivedFrom":sQuery(id+"F0.wireOp",EDGE,"E11")}),-1.0]])]});
            var Q1;
            Q1=makeQuery(id+"F0.imprint","IMPRINT",FACE,{"disambiguationData":[TD([[makeQuery(id+"F0.imprint","IMPRINT",EDGE,{"derivedFrom":sQuery(id+"F0.wireOp",EDGE,"E14")}),-1.0]])]});
            extrude(context, id + "F2", {"entities" : qUnion([Q0, Q1]), "operationType" : NewBodyOperationType.ADD, "depth" : 4.4 * mm});
        }
        {
            var Q0;
            Q0=makeQuery(id+"F0.imprint","IMPRINT",FACE,{"disambiguationData":[TD([[makeQuery(id+"F0.imprint","IMPRINT",EDGE,{"derivedFrom":sQuery(id+"F0.wireOp",EDGE,"E5.bottom")}),1.0]])]});
            var Q1;
            Q1=makeQuery(id+"F0.imprint","IMPRINT",FACE,{"disambiguationData":[TD([[makeQuery(id+"F0.imprint","IMPRINT",EDGE,{"derivedFrom":sQuery(id+"F0.wireOp",EDGE,"E6.bottom")}),1.0]])]});
            extrude(context, id + "F3", {"entities" : qUnion([Q0, Q1]), "operationType" : NewBodyOperationType.ADD, "depth" : 1.5 * mm});
        }
        {
            var Q0;
            Q0=makeQuery(id+"F0.imprint","IMPRINT",FACE,{"disambiguationData":[TD([[makeQuery(id+"F0.imprint","IMPRINT",EDGE,{"derivedFrom":sQuery(id+"F0.wireOp",EDGE,"E4.bottom")}),1.0]])]});
            extrude(context, id + "F4", {"entities" : qUnion([Q0]), "operationType" : NewBodyOperationType.ADD, "depth" : 4.3 * mm});
        }
        {
            var Q0;
            Q0=makeQuery(id+"F0.imprint","IMPRINT",FACE,{"disambiguationData":[TD([[makeQuery(id+"F0.imprint","IMPRINT",EDGE,{"derivedFrom":sQuery(id+"F0.wireOp",EDGE,"E8.bottom")}),1.0]])]});
            var Q1;
            Q1=makeQuery(id+"F0.imprint","IMPRINT",FACE,{"disambiguationData":[TD([[makeQuery(id+"F0.imprint","IMPRINT",EDGE,{"derivedFrom":sQuery(id+"F0.wireOp",EDGE,"E7.bottom")}),1.0]])]});
            var Q2;
            Q2=makeQuery(id+"F0.imprint","IMPRINT",FACE,{"disambiguationData":[TD([[makeQuery(id+"F0.imprint","IMPRINT",EDGE,{"derivedFrom":sQuery(id+"F0.wireOp",EDGE,"E9.bottom")}),1.0]])]});
            extrude(context, id + "F5", {"entities" : qUnion([Q0, Q1, Q2]), "operationType" : NewBodyOperationType.ADD, "depth" : 5 * mm});
        }
        {
            var Q0;
            Q0=makeQuery(id+"F0.imprint","IMPRINT",FACE,{"disambiguationData":[TD([[makeQuery(id+"F0.imprint","IMPRINT",EDGE,{"derivedFrom":sQuery(id+"F0.wireOp",EDGE,"E10.bottom")}),1.0]])]});
            extrude(context, id + "F6", {"entities" : qUnion([Q0]), "operationType" : NewBodyOperationType.ADD, "depth" : 13.6 * mm});
        }
    });
